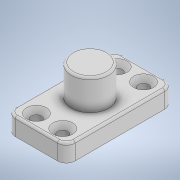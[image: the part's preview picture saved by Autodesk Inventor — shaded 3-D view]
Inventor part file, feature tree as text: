
AUTODESK INVENTOR PART (.ipt)
format: ipt  version: 2020.3 (Build 243373000, 373)  size: 176,128 bytes
history: native  units: mm
features: extrude x3, sketch x2, fillet x2, hole x1
ambient origin geometry x8: Origin, YZ Plane, XZ Plane, XY Plane, X Axis, Y Axis, Z Axis, Center Point
bodies: Solid1 (feature_tree)
feature tree (8):
  sketch  "Sketch1"  dims[d0=24.6mm d1=12.4mm]
  extrude  "Extrusion1"  Depth=12.4mm
  extrude  "Extrusion2"  Depth=2.0mm
  fillet  "Fillet1"  Radius=4.0mm
  extrude  "Extrusion3"  Depth=4.0mm TaperAngle=0.0deg
  fillet  "Fillet2"  Radius=2.0mm
  hole  "Hole2"  [1 undecoded]
  sketch  "Sketch3"  dims[d2=6.0mm d4=6.0mm d5=4.0mm d6=0.0mm d7=4.0mm d8=0.0mm d16=2.0mm d17=8.5mm d18=11.0mm d19=0.0mm d20=0.5mm d21=6.8mm d28=2.3mm d29=6.0mm d30=4.5mm d31=2.0mm d32=90.0deg d33=6.5mm d34=0.0mm]
note: 1 required parameter value undecoded (feature->parameter linkage not recoverable at this tier; creation-order binding heuristic only, values carry confidence <= 0.55)
